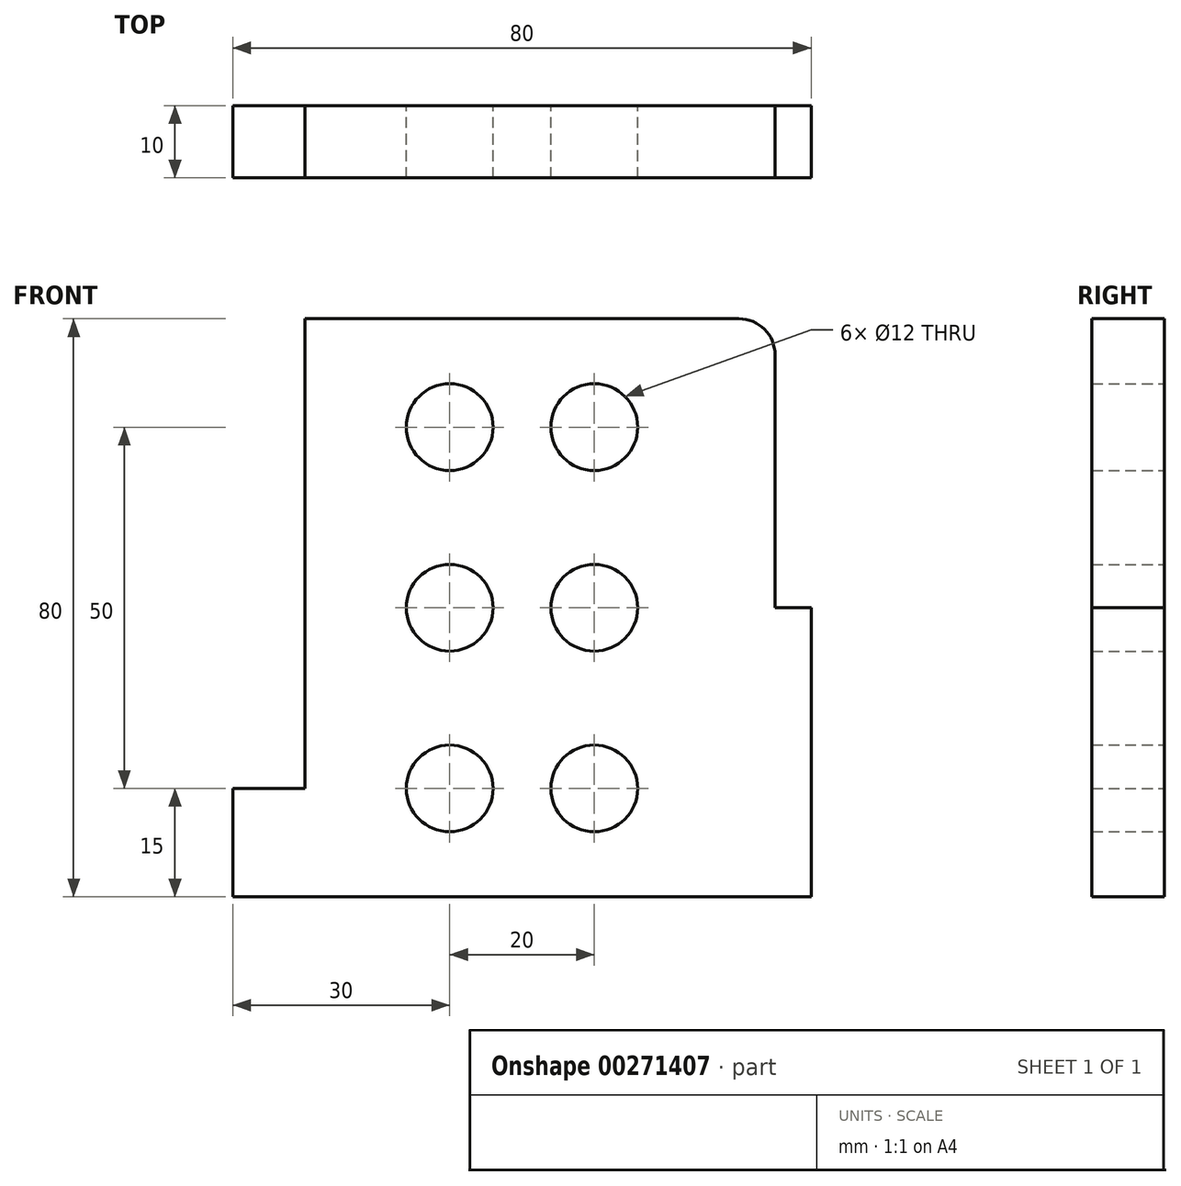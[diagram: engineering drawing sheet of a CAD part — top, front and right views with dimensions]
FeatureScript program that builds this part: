
annotation { "Feature Type Name" : "Feature", "Feature Type Description" : "" }
export const myFeature = defineFeature(function(context is Context, id is Id, definition is map)
    precondition{}
    {
        {
            var Q0;
            Q0=qCreatedBy(makeId("Front.planeOp"),FACE);
            var sketch = newSketch(context, id + "F0", { "sketchPlane" : qUnion([Q0])});
            skLineSegment(sketch, "E0", {"start": v(0, 0) * mm, "end": v(0, 15) * mm});
            skLineSegment(sketch, "E1", {"start": v(0, 15) * mm, "end": v(10, 15) * mm});
            skLineSegment(sketch, "E2", {"start": v(10, 15) * mm, "end": v(10, 80) * mm});
            skLineSegment(sketch, "E3", {"start": v(10, 80) * mm, "end": v(70, 80) * mm});
            skArc(sketch, "E4", {"start": v(75, 75) * mm, "mid": v(73.54, 78.54) * mm, "end": v(70, 80) * mm});
            skLineSegment(sketch, "E5", {"start": v(75, 75) * mm, "end": v(75, 40) * mm});
            skLineSegment(sketch, "E6", {"start": v(75, 40) * mm, "end": v(80, 40) * mm});
            skLineSegment(sketch, "E7", {"start": v(80, 40) * mm, "end": v(80, 0) * mm});
            skLineSegment(sketch, "E8", {"start": v(80, 0) * mm, "end": v(0, 0) * mm});
            skLineSegment(sketch, "E9.bottom", {"start": v(30, 65) * mm, "end": v(50, 65) * mm, "construction": true});
            skLineSegment(sketch, "E9.top", {"start": v(30, 15) * mm, "end": v(50, 15) * mm, "construction": true});
            skLineSegment(sketch, "E9.left", {"start": v(30, 65) * mm, "end": v(30, 15) * mm, "construction": true});
            skLineSegment(sketch, "E9.right", {"start": v(50, 65) * mm, "end": v(50, 15) * mm, "construction": true});
            skLineSegment(sketch, "E10", {"start": v(30, 40) * mm, "end": v(50, 40) * mm, "construction": true});
            skCircle(sketch, "E11", {"center": v(30, 65) * mm, "radius": 6 * mm});
            skCircle(sketch, "E12", {"center": v(50, 65) * mm, "radius": 6 * mm});
            skCircle(sketch, "E13", {"center": v(30, 40) * mm, "radius": 6 * mm});
            skCircle(sketch, "E14", {"center": v(50, 40) * mm, "radius": 6 * mm});
            skCircle(sketch, "E15", {"center": v(30, 15) * mm, "radius": 6 * mm});
            skCircle(sketch, "E16", {"center": v(50, 15) * mm, "radius": 6 * mm});
            skSolve(sketch);
        }
        {
            var Q0;
            Q0 = qSketchRegion(id + "F0", true);
            extrude(context, id + "F1", {"entities" : qUnion([Q0]), "depth" : 10 * mm});
        }
    });
